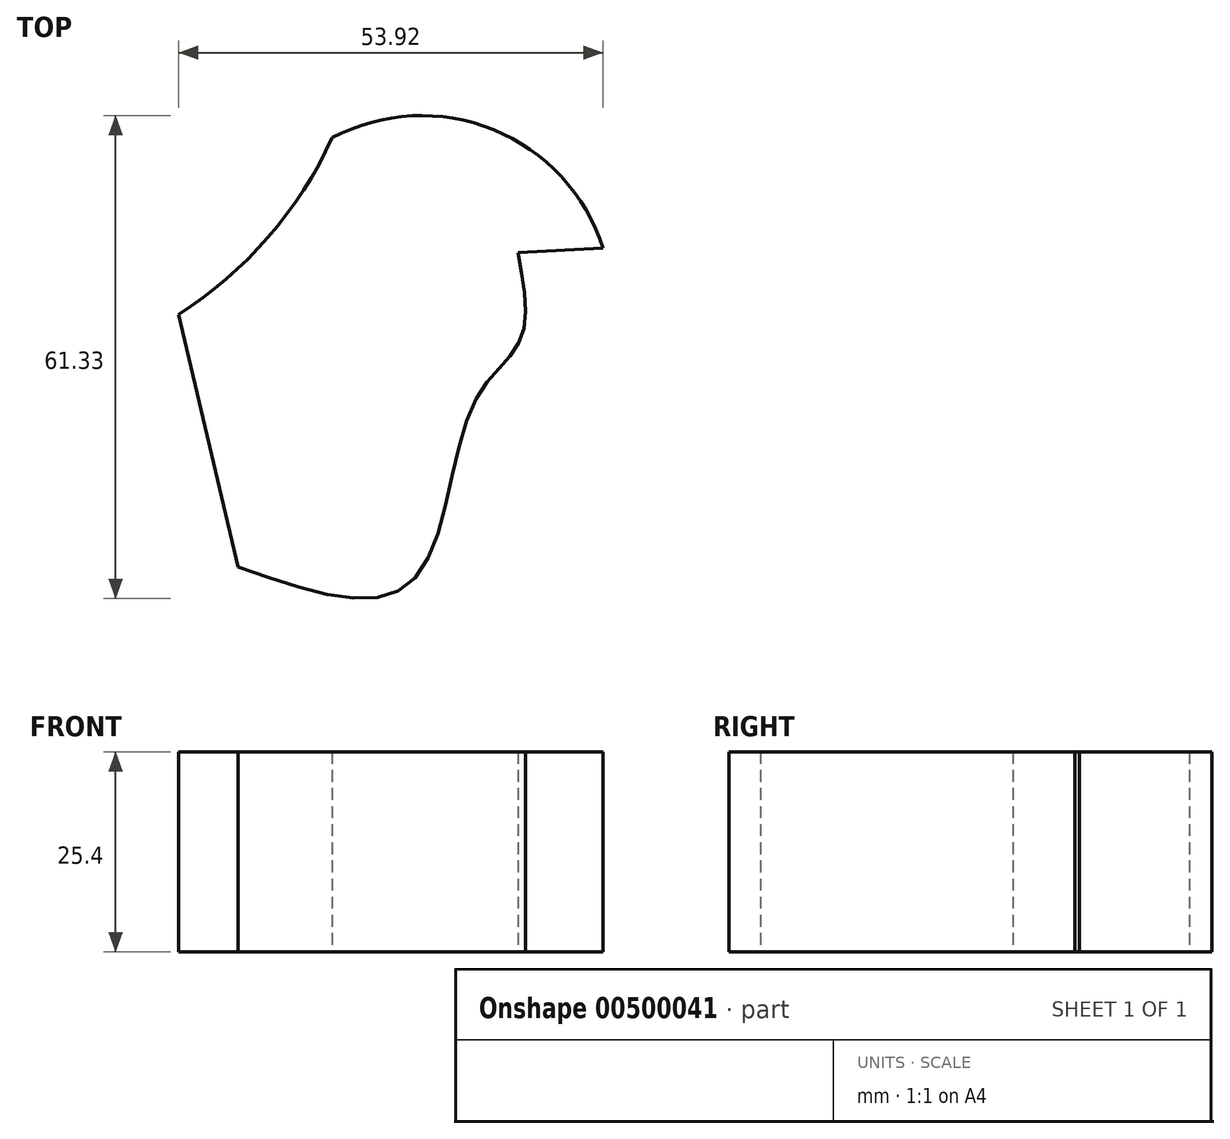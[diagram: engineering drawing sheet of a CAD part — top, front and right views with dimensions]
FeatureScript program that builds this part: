
annotation { "Feature Type Name" : "Feature", "Feature Type Description" : "" }
export const myFeature = defineFeature(function(context is Context, id is Id, definition is map)
    precondition{}
    {
        {
            var Q0;
            Q0=qCreatedBy(makeId("Top.planeOp"),FACE);
            var sketch = newSketch(context, id + "F0", { "sketchPlane" : qUnion([Q0])});
            skArc(sketch, "E0", {"start": v(34.4, 22.59) * mm, "mid": v(20.46, 37.62) * mm, "end": v(0, 36.58) * mm});
            skArc(sketch, "E1", {"start": v(-19.53, 14.14) * mm, "mid": v(-8.14, 23.95) * mm, "end": v(0, 36.58) * mm});
            skLineSegment(sketch, "E2", {"start": v(-19.53, 14.14) * mm, "end": v(-11.95, -17.93) * mm});
            skFitSpline(sketch, "E3", {"points": [v(-11.95, -17.93) * mm, v(9.91, -19.97) * mm, v(17.78, 2.48) * mm, v(23.9, 10.93) * mm, v(23.6, 22) * mm], "startDerivative": vector(89.37, -31.6) * mm, "endDerivative": vector(-10.96, 59.76) * mm});
            skLineSegment(sketch, "E4", {"start": v(23.6, 22) * mm, "end": v(34.4, 22.59) * mm});
            skSolve(sketch);
        }
        {
            var Q0;
            Q0=makeQuery(id+"F0.imprint","IMPRINT",FACE,{"disambiguationData":[TD([[makeQuery(id+"F0.imprint","IMPRINT",EDGE,{"derivedFrom":sQuery(id+"F0.wireOp",EDGE,"E0")}),1.0]])]});
            extrude(context, id + "F1", {"entities" : qUnion([Q0]), "endBound" : BoundingType.SYMMETRIC, "depth" : 25.4 * mm});
        }
    });
